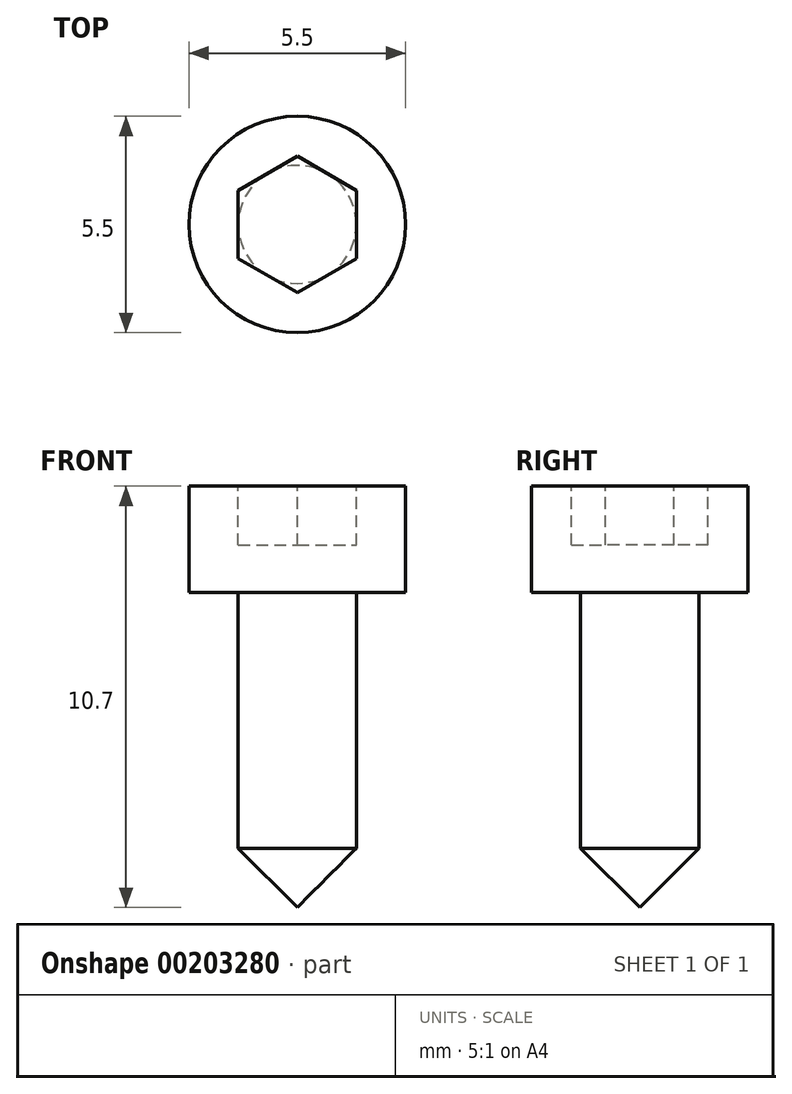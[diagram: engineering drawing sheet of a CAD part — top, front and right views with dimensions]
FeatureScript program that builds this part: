
annotation { "Feature Type Name" : "Feature", "Feature Type Description" : "" }
export const myFeature = defineFeature(function(context is Context, id is Id, definition is map)
    precondition{}
    {
        {
            var Q0;
            Q0=qCreatedBy(makeId("Top.planeOp"),FACE);
            var sketch = newSketch(context, id + "F0", { "sketchPlane" : qUnion([Q0])});
            skCircle(sketch, "E0", {"center": v(0, 0) * mm, "radius": 2.75 * mm});
            skCircle(sketch, "E1", {"center": v(0, 0) * mm, "radius": 1.5 * mm});
            skSolve(sketch);
        }
        {
            var Q0;
            Q0 = qSketchRegion(id + "F0", true);
            var Q1;
            Q1=makeQuery(id+"F0.imprint","IMPRINT",FACE,{"disambiguationData":[TD([[makeQuery(id+"F0.imprint","IMPRINT",EDGE,{"derivedFrom":sQuery(id+"F0.wireOp",EDGE,"E1")}),1.0]])]});
            extrude(context, id + "F1", {"entities" : qUnion([Q0, Q1]), "depth" : 2.7 * mm});
        }
        {
            var Q0;
            Q0=makeQuery(id+"F0.imprint","IMPRINT",FACE,{"disambiguationData":[TD([[makeQuery(id+"F0.imprint","IMPRINT",EDGE,{"derivedFrom":sQuery(id+"F0.wireOp",EDGE,"E1")}),1.0]])]});
            extrude(context, id + "F2", {"entities" : qUnion([Q0]), "operationType" : NewBodyOperationType.ADD, "oppositeDirection" : true, "depth" : 8 * mm});
        }
        {
            var Q0;
            Q0=makeQuery(id+"F2.opExtrude","CAP_EDGE",EDGE,{"disambiguationData":[OSD([sQuery(id+"F0.wireOp",EDGE,"E1")])],"isStart":false});
            chamfer(context, id + "F3", {"entities" : qUnion([Q0]), "width" : 1.5 * mm, "tangentPropagation" : true});
        }
        {
            var Q0;
            Q0=makeQuery(id+"F1.opExtrude","CAP_FACE",FACE,{"disambiguationData":[OSD([sQuery(id+"F0.wireOp",EDGE,"E0")])],"isStart":false});
            var sketch = newSketch(context, id + "F4", { "sketchPlane" : qUnion([Q0])});
            skCircle(sketch, "E2.cCircle", {"center": v(0, 0) * mm, "radius": 1.5 * mm, "construction": true});
            skLineSegment(sketch, "E2.0", {"start": v(1.5, 0.87) * mm, "end": v(1.5, -0.87) * mm});
            skLineSegment(sketch, "E2.1", {"start": v(1.5, -0.87) * mm, "end": v(0, -1.73) * mm});
            skLineSegment(sketch, "E2.2", {"start": v(0, -1.73) * mm, "end": v(-1.5, -0.87) * mm});
            skLineSegment(sketch, "E2.3", {"start": v(-1.5, -0.87) * mm, "end": v(-1.5, 0.87) * mm});
            skLineSegment(sketch, "E2.4", {"start": v(-1.5, 0.87) * mm, "end": v(0, 1.73) * mm});
            skLineSegment(sketch, "E2.5", {"start": v(0, 1.73) * mm, "end": v(1.5, 0.87) * mm});
            skPoint(sketch, "E2.0.midPoint", {"position": v(1.5, 0) * mm});
            skSolve(sketch);
        }
        {
            var Q0;
            Q0=makeQuery(id+"F4.imprint","IMPRINT",FACE,{"disambiguationData":[TD([[makeQuery(id+"F4.imprint","IMPRINT",EDGE,{"derivedFrom":sQuery(id+"F4.wireOp",EDGE,"E2.0")}),-1.0]])]});
            extrude(context, id + "F5", {"entities" : qUnion([Q0]), "operationType" : NewBodyOperationType.REMOVE, "oppositeDirection" : true, "depth" : 1.5 * mm});
        }
    });
